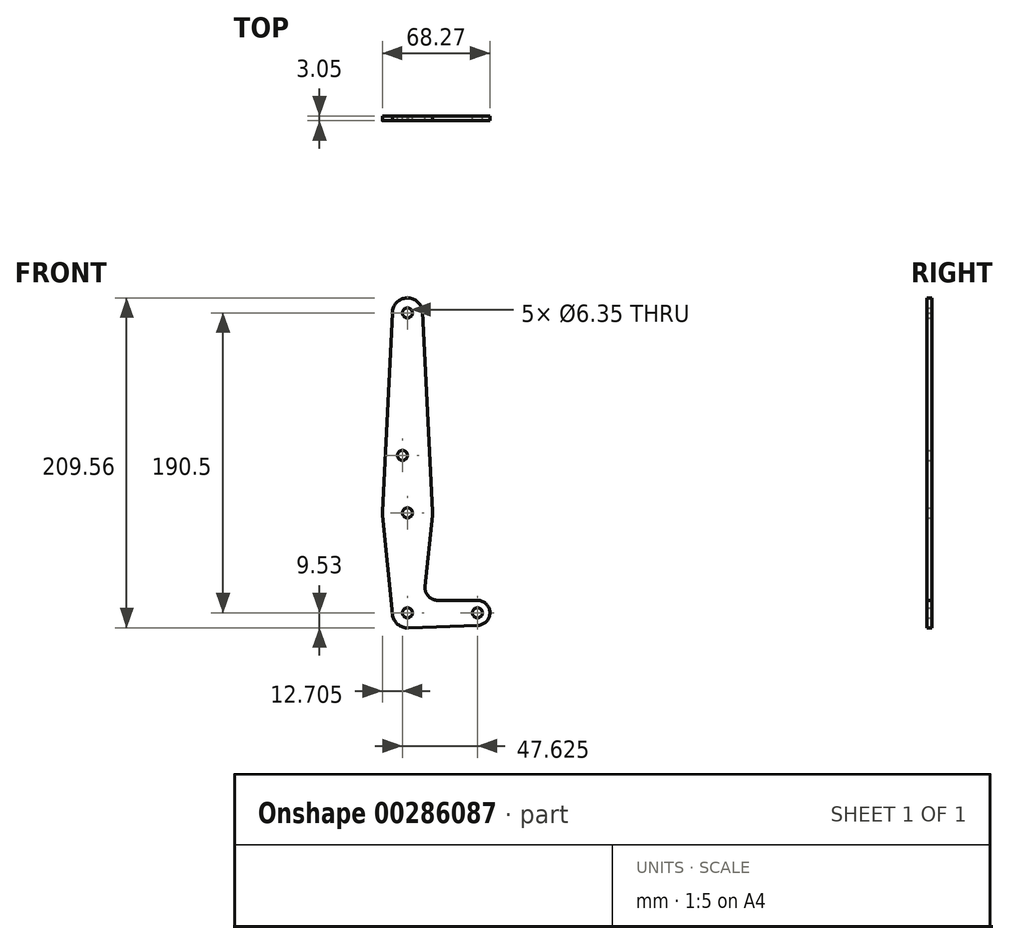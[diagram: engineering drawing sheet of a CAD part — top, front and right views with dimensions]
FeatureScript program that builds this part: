
annotation { "Feature Type Name" : "Feature", "Feature Type Description" : "" }
export const myFeature = defineFeature(function(context is Context, id is Id, definition is map)
    precondition{}
    {
        {
            var Q0;
            Q0=qCreatedBy(makeId("Front.planeOp"),FACE);
            var sketch = newSketch(context, id + "F0", { "sketchPlane" : qUnion([Q0])});
            skCircle(sketch, "E0", {"center": v(0, 190.5) * mm, "radius": 9.53 * mm});
            skCircle(sketch, "E1", {"center": v(0, 63.5) * mm, "radius": 15.88 * mm});
            skCircle(sketch, "E2", {"center": v(0, 0) * mm, "radius": 9.53 * mm});
            skCircle(sketch, "E3", {"center": v(44.45, 0) * mm, "radius": 7.94 * mm});
            skLineSegment(sketch, "E4", {"start": v(0, 190.5) * mm, "end": v(0, 63.5) * mm, "construction": true});
            skLineSegment(sketch, "E5", {"start": v(0, 63.5) * mm, "end": v(0, 0) * mm, "construction": true});
            skLineSegment(sketch, "E6", {"start": v(0, 0) * mm, "end": v(44.45, 0) * mm, "construction": true});
            skLineSegment(sketch, "E7", {"start": v(-9.53, 190.5) * mm, "end": v(-15.86, 64.3) * mm});
            skLineSegment(sketch, "E8", {"start": v(9.51, 190.98) * mm, "end": v(15.86, 64.3) * mm});
            skLineSegment(sketch, "E9", {"start": v(19.16, 7.94) * mm, "end": v(44.45, 7.94) * mm});
            skLineSegment(sketch, "E10", {"start": v(0, -9.53) * mm, "end": v(44.73, -7.93) * mm});
            skCircle(sketch, "E11", {"center": v(0, 190.5) * mm, "radius": 3.18 * mm});
            skCircle(sketch, "E12", {"center": v(0, 63.5) * mm, "radius": 3.18 * mm});
            skCircle(sketch, "E13", {"center": v(0, 0) * mm, "radius": 3.18 * mm});
            skCircle(sketch, "E14", {"center": v(44.45, 0) * mm, "radius": 3.18 * mm});
            skCircle(sketch, "E15", {"center": v(-3.17, 100.03) * mm, "radius": 3.18 * mm});
            skLineSegment(sketch, "E16", {"start": v(-15.8, 61.91) * mm, "end": v(-9.48, -0.95) * mm});
            skLineSegment(sketch, "E17", {"start": v(15.8, 61.91) * mm, "end": v(11.25, 16.68) * mm});
            skArc(sketch, "E18.filletArc", {"start": v(11.25, 16.68) * mm, "mid": v(13.26, 10.55) * mm, "end": v(19.16, 7.94) * mm});
            skSolve(sketch);
        }
        {
            var Q0;
            Q0 = qSketchRegion(id + "F0", true);
            extrude(context, id + "F1", {"entities" : qUnion([Q0]), "depth" : 3.05 * mm});
        }
    });
